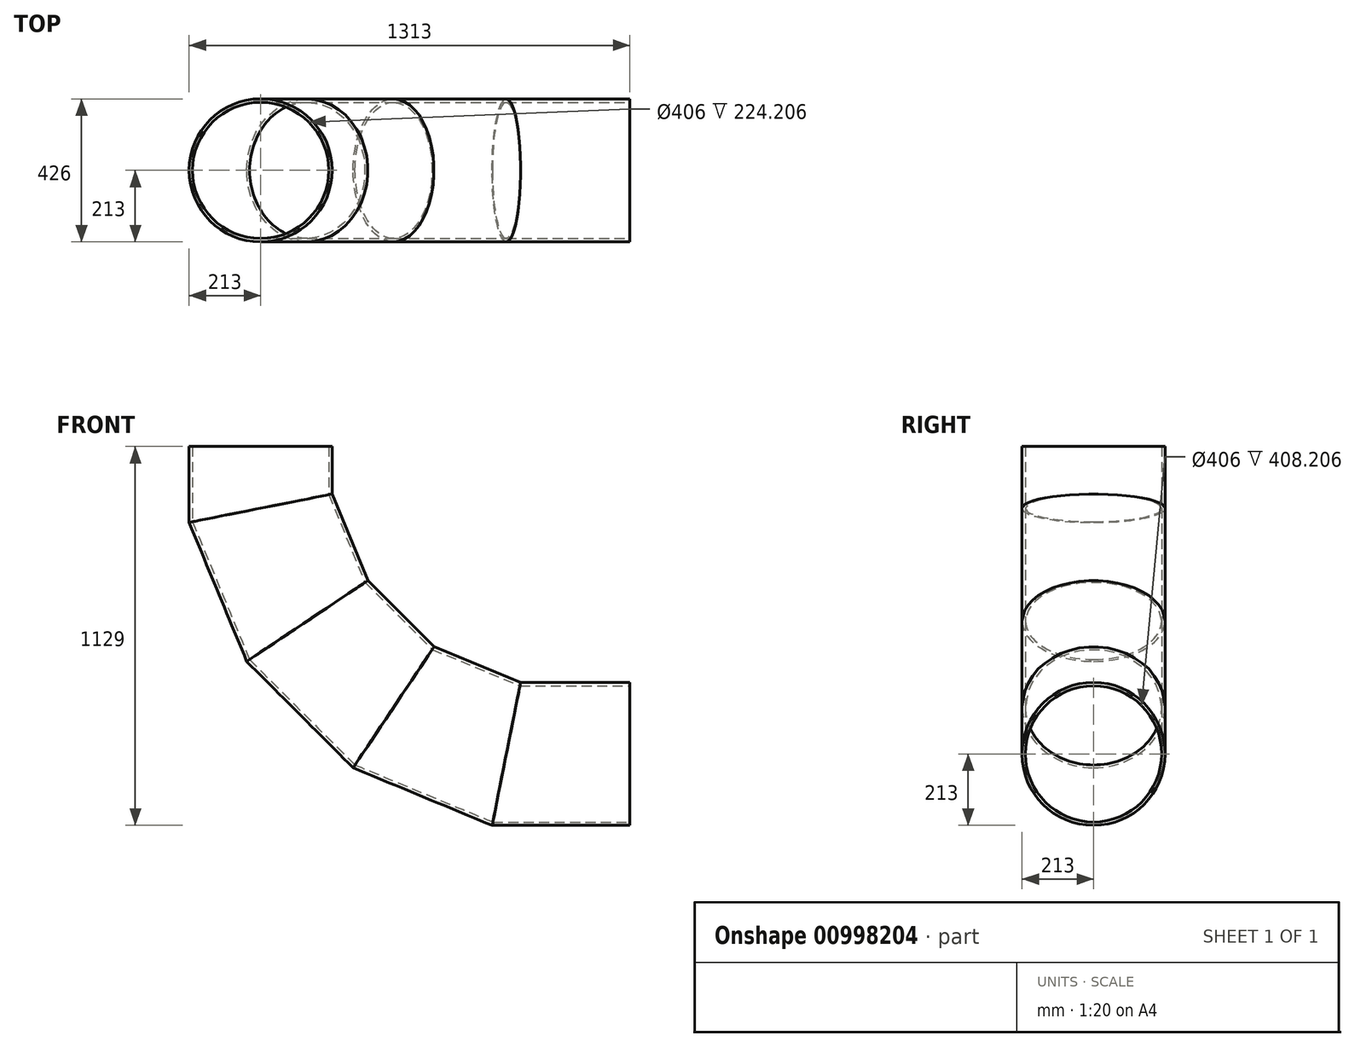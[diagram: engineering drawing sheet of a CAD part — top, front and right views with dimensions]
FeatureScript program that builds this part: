
annotation { "Feature Type Name" : "Feature", "Feature Type Description" : "" }
export const myFeature = defineFeature(function(context is Context, id is Id, definition is map)
    precondition{}
    {
        {
            var Q0;
            Q0=qCreatedBy(makeId("Front.planeOp"),FACE);
            var sketch = newSketch(context, id + "F0", { "sketchPlane" : qUnion([Q0])});
            skLineSegment(sketch, "E0", {"start": v(0, 0) * mm, "end": v(0, -183.8) * mm});
            skLineSegment(sketch, "E1", {"start": v(0, -183.8) * mm, "end": v(139.15, -519.74) * mm});
            skLineSegment(sketch, "E2", {"start": v(139.15, -519.74) * mm, "end": v(396.26, -776.85) * mm});
            skLineSegment(sketch, "E3", {"start": v(396.26, -776.85) * mm, "end": v(732.2, -916) * mm});
            skLineSegment(sketch, "E4", {"start": v(732.2, -916) * mm, "end": v(1100, -916) * mm});
            skLineSegment(sketch, "E5", {"start": v(69.57, -351.77) * mm, "end": v(914, -2) * mm, "construction": true});
            skLineSegment(sketch, "E6", {"start": v(914, -2) * mm, "end": v(267.7, -648.3) * mm, "construction": true});
            skLineSegment(sketch, "E7", {"start": v(914, -2) * mm, "end": v(564.23, -846.43) * mm, "construction": true});
            skLineSegment(sketch, "E8", {"start": v(914, -2) * mm, "end": v(0, -2) * mm, "construction": true});
            skSolve(sketch);
        }
        {
            var Q0;
            Q0=qCreatedBy(makeId("Top.planeOp"),FACE);
            var sketch = newSketch(context, id + "F1", { "sketchPlane" : qUnion([Q0])});
            skCircle(sketch, "E9", {"center": v(0, 0) * mm, "radius": 203 * mm});
            skCircle(sketch, "E10", {"center": v(0, 0) * mm, "radius": 213 * mm});
            skSolve(sketch);
        }
        {
            var Q0;
            Q0=makeQuery(id+"F1.imprint","IMPRINT",FACE,{"disambiguationData":[TD([[makeQuery(id+"F1.imprint","IMPRINT",EDGE,{"derivedFrom":sQuery(id+"F1.wireOp",EDGE,"E9")}),-1.0]])]});
            var Q1;
            Q1=sQuery(id+"F0.wireOp",EDGE,"E0");
            var Q2;
            Q2=sQuery(id+"F0.wireOp",EDGE,"E1");
            var Q3;
            Q3=sQuery(id+"F0.wireOp",EDGE,"E2");
            var Q4;
            Q4=sQuery(id+"F0.wireOp",EDGE,"E3");
            var Q5;
            Q5=sQuery(id+"F0.wireOp",EDGE,"E4");
            sweep(context, id + "F2", {"profiles" : qUnion([Q0]), "path" : qUnion([Q1, Q2, Q3, Q4, Q5])});
        }
    });
